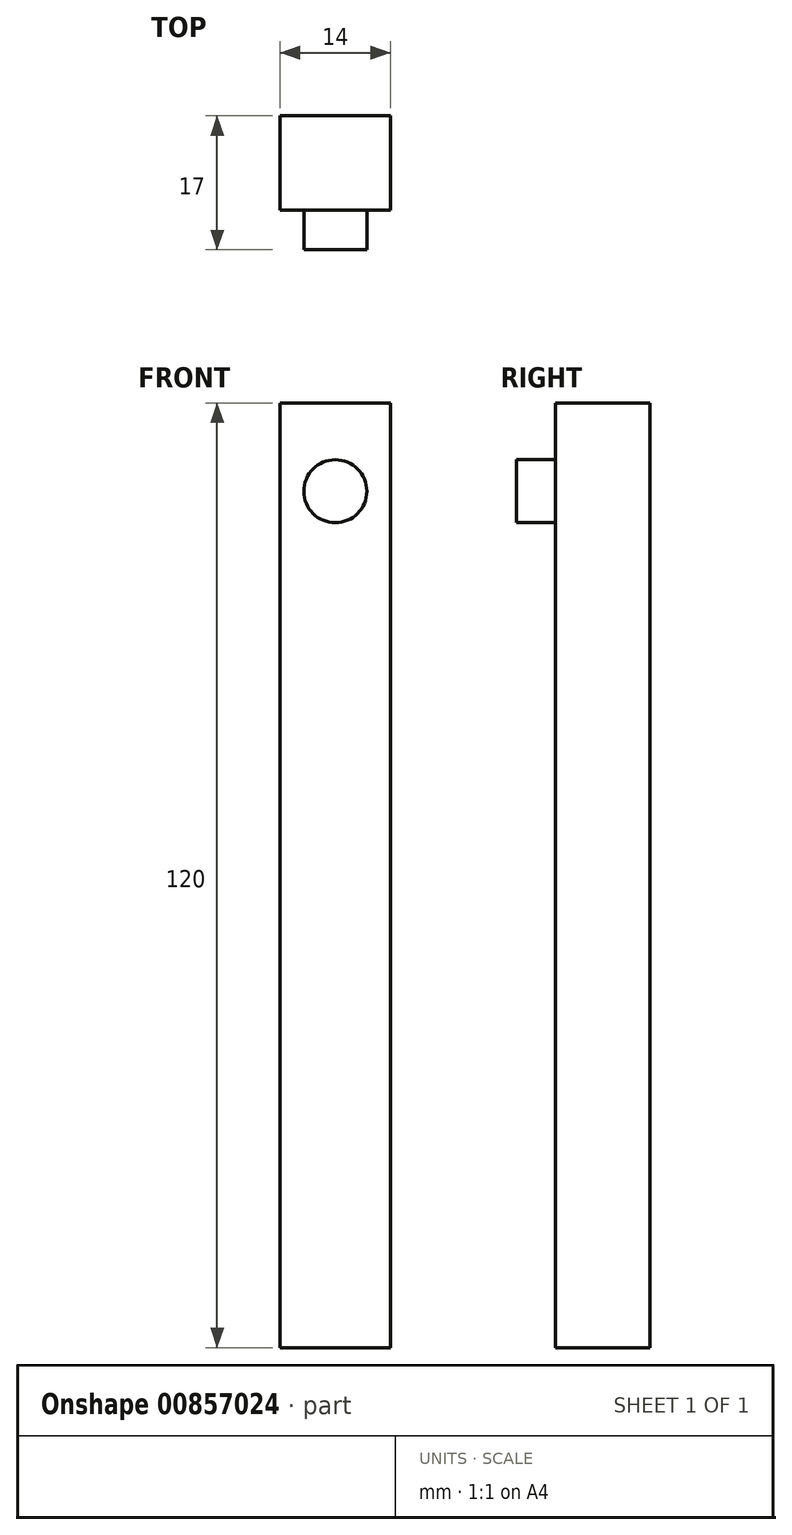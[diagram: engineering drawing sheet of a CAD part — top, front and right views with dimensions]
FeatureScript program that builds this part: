
annotation { "Feature Type Name" : "Feature", "Feature Type Description" : "" }
export const myFeature = defineFeature(function(context is Context, id is Id, definition is map)
    precondition{}
    {
        {
            var Q0;
            Q0=qCreatedBy(makeId("Top.planeOp"),FACE);
            var sketch = newSketch(context, id + "F0", { "sketchPlane" : qUnion([Q0])});
            skLineSegment(sketch, "E0.bottom", {"start": v(-7, 6) * mm, "end": v(7, 6) * mm});
            skLineSegment(sketch, "E0.top", {"start": v(-7, -6) * mm, "end": v(7, -6) * mm});
            skLineSegment(sketch, "E0.left", {"start": v(-7, 6) * mm, "end": v(-7, -6) * mm});
            skLineSegment(sketch, "E0.right", {"start": v(7, 6) * mm, "end": v(7, -6) * mm});
            skPoint(sketch, "E0.middle", {"position": v(0, 0) * mm});
            skSolve(sketch);
        }
        {
            var Q0;
            Q0 = qSketchRegion(id + "F0", true);
            extrude(context, id + "F1", {"entities" : qUnion([Q0]), "depth" : 120 * mm, "offsetDistance" : 25 * mm});
        }
        {
            var Q0;
            Q0=makeQuery(id+"F1.opExtrude","SWEPT_FACE",FACE,{"disambiguationData":[OSD([sQuery(id+"F0.wireOp",EDGE,"E0.top")])]});
            var sketch = newSketch(context, id + "F2", { "sketchPlane" : qUnion([Q0])});
            skCircle(sketch, "E1", {"center": v(0, 108.8) * mm, "radius": 4 * mm});
            skSolve(sketch);
        }
        {
            var Q0;
            Q0 = qSketchRegion(id + "F2", true);
            extrude(context, id + "F3", {"entities" : qUnion([Q0]), "operationType" : NewBodyOperationType.ADD, "depth" : 5 * mm, "offsetDistance" : 25 * mm});
        }
    });
